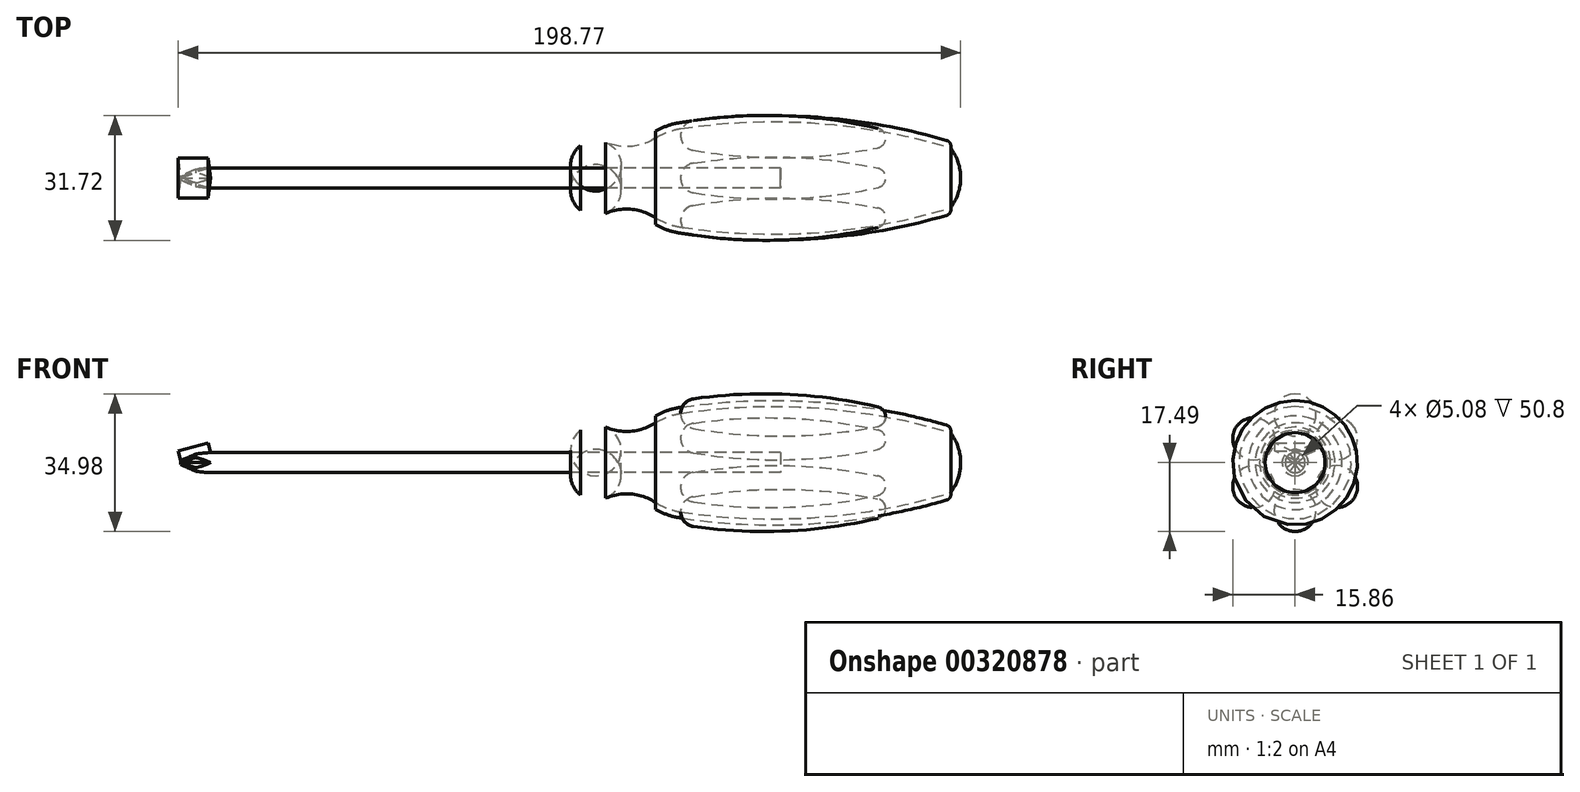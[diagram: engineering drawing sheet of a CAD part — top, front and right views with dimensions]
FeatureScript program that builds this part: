
annotation { "Feature Type Name" : "Feature", "Feature Type Description" : "" }
export const myFeature = defineFeature(function(context is Context, id is Id, definition is map)
    precondition{}
    {
        {
            var Q0;
            Q0=qCreatedBy(makeId("Front.planeOp"),FACE);
            var sketch = newSketch(context, id + "F0", { "sketchPlane" : qUnion([Q0])});
            skLineSegment(sketch, "E0", {"start": v(-101.6, 0) * mm, "end": v(96.52, 0) * mm});
            skLineSegment(sketch, "E1", {"start": v(96.52, 0) * mm, "end": v(117.55, 0) * mm, "construction": true});
            skLineSegment(sketch, "E2", {"start": v(50.8, 2.54) * mm, "end": v(-97.8, 2.54) * mm});
            skLineSegment(sketch, "E3", {"start": v(-101.6, 0.5) * mm, "end": v(-101.6, 0) * mm});
            skLineSegment(sketch, "E4", {"start": v(0, 2.54) * mm, "end": v(0, 8.25) * mm});
            skArc(sketch, "E5", {"start": v(6.35, 9.02) * mm, "mid": v(3.07, 9.48) * mm, "end": v(0, 8.25) * mm});
            skArc(sketch, "E6", {"start": v(6.35, 9.02) * mm, "mid": v(12.84, 7.99) * mm, "end": v(19.05, 10.11) * mm});
            skArc(sketch, "E7", {"start": v(25.4, 12.52) * mm, "mid": v(22.1, 11.65) * mm, "end": v(19.05, 10.11) * mm});
            skArc(sketch, "E8", {"start": v(93.98, 7.62) * mm, "mid": v(59.96, 13.9) * mm, "end": v(25.4, 12.52) * mm});
            skArc(sketch, "E9", {"start": v(96.52, 0) * mm, "mid": v(95.87, 4.02) * mm, "end": v(93.98, 7.62) * mm});
            skArc(sketch, "E10.0", {"start": v(25.17, 14.02) * mm, "mid": v(22.01, 13.24) * mm, "end": v(19.05, 11.9) * mm});
            skArc(sketch, "E10.1", {"start": v(92.95, 9.52) * mm, "mid": v(59.3, 15.46) * mm, "end": v(25.17, 14.02) * mm});
            skLineSegment(sketch, "E11", {"start": v(19.05, 11.9) * mm, "end": v(19.05, 10.11) * mm});
            skArc(sketch, "E12", {"start": v(93.98, 7.62) * mm, "mid": v(93.86, 8.78) * mm, "end": v(92.95, 9.52) * mm});
            skPoint(sketch, "E13.orphan", {"position": v(0, 0) * mm});
            skLineSegment(sketch, "E14", {"start": v(50.8, 2.54) * mm, "end": v(50.8, 0) * mm});
            skLineSegment(sketch, "E15", {"start": v(-101.6, 0.5) * mm, "end": v(-97.8, 2.54) * mm});
            skPoint(sketch, "E16.orphan", {"position": v(-101.6, 2.54) * mm});
            skSolve(sketch);
        }
        {
            var Q0;
            Q0=qCreatedBy(makeId("Front.planeOp"),FACE);
            var sketch = newSketch(context, id + "F1", { "sketchPlane" : qUnion([Q0])});
            skLineSegment(sketch, "E17", {"start": v(25.4, 12.52) * mm, "end": v(77.47, 11.64) * mm});
            skArc(sketch, "E18", {"start": v(28.67, 16.22) * mm, "mid": v(26.35, 14.97) * mm, "end": v(25.4, 12.52) * mm});
            skArc(sketch, "E19", {"start": v(77.47, 11.64) * mm, "mid": v(76.93, 13.25) * mm, "end": v(75.5, 14.16) * mm});
            skArc(sketch, "E20", {"start": v(75.5, 14.16) * mm, "mid": v(52.19, 17.37) * mm, "end": v(28.67, 16.22) * mm});
            skSolve(sketch);
        }
        {
            var Q0;
            Q0=qCreatedBy(makeId("Front.planeOp"),FACE);
            var sketch = newSketch(context, id + "F2", { "sketchPlane" : qUnion([Q0])});
            skLineSegment(sketch, "E21", {"start": v(-101.6, 0.5) * mm, "end": v(-93.98, 2.54) * mm});
            skSolve(sketch);
        }
        {
            var Q0;
            Q0=sQuery(id+"F2.wireOp",VERTEX,"E21.start");
            var Q1;
            Q1=sQuery(id+"F2.wireOp",EDGE,"E21");
            cPlane(context, id + "F3", {"entities" : qUnion([Q0, Q1]), "cplaneType" : CPlaneType.LINE_POINT, "offset" : 25.4 * mm, "width" : 152.4 * mm, "height" : 152.4 * mm});
        }
        {
            var Q0;
            Q0=qCreatedBy(id+"F3.planeOp",FACE);
            var sketch = newSketch(context, id + "F4", { "sketchPlane" : qUnion([Q0])});
            skLineSegment(sketch, "E22", {"start": v(5.08, 29.2) * mm, "end": v(0, 26.67) * mm});
            skLineSegment(sketch, "E23", {"start": v(0, 26.67) * mm, "end": v(-5.08, 29.2) * mm});
            skLineSegment(sketch, "E24", {"start": v(-5.08, 29.2) * mm, "end": v(5.08, 29.2) * mm});
            skLineSegment(sketch, "E25", {"start": v(0, 29.2) * mm, "end": v(0, 26.67) * mm, "construction": true});
            skSolve(sketch);
        }
        {
            var Q0;
            {var subQ0=sQuery(id+"F0.wireOp",EDGE,"E3");Q0=makeQuery(id+"F0.imprint","IMPRINT",FACE,{"disambiguationData":[TD([[makeQuery(id+"F0.imprint","IMPRINT",EDGE,{"derivedFrom":subQ0}),1.0]])]});}
            var Q1;
            Q1=sQuery(id+"F0.wireOp",EDGE,"E1");
            revolve(context, id + "F5", {"entities" : qUnion([Q0]), "axis" : qUnion([Q1]), "revolveType" : RevolveType.FULL});
        }
        {
            var Q0;
            {var subQ0=sQuery(id+"F0.wireOp",EDGE,"E4");Q0=makeQuery(id+"F0.imprint","IMPRINT",FACE,{"disambiguationData":[TD([[makeQuery(id+"F0.imprint","IMPRINT",EDGE,{"derivedFrom":subQ0}),-1.0]])]});}
            var Q1;
            Q1=sQuery(id+"F0.wireOp",EDGE,"E1");
            revolve(context, id + "F6", {"entities" : qUnion([Q0]), "axis" : qUnion([Q1]), "revolveType" : RevolveType.FULL});
        }
        {
            var Q0;
            Q0=makeQuery(id+"F1.imprint","IMPRINT",FACE,{"disambiguationData":[TD([[makeQuery(id+"F1.imprint","IMPRINT",EDGE,{"derivedFrom":sQuery(id+"F1.wireOp",EDGE,"E17")}),1.0]])]});
            var Q1;
            Q1=sQuery(id+"F1.wireOp",EDGE,"E17");
            revolve(context, id + "F7", {"entities" : qUnion([Q0]), "axis" : qUnion([Q1]), "revolveType" : RevolveType.FULL});
        }
        {
            var Q0;
            Q0=makeQuery(id+"F7.opRevolve","SWEPT_BODY",BODY,{"disambiguationData":[OSD([sQuery(id+"F1.wireOp",EDGE,"E17"),sQuery(id+"F1.wireOp",EDGE,"E18"),sQuery(id+"F1.wireOp",EDGE,"E19"),sQuery(id+"F1.wireOp",EDGE,"E20")])]});
            var Q1;
            Q1=sQuery(id+"F0.wireOp",EDGE,"E1");
            circularPattern(context, id + "F8", {"entities" : qUnion([Q0]), "axis" : qUnion([Q1]), "angle" : 360 * degree, "instanceCount" : 6, "equalSpace" : true});
        }
        {
            var Q0;
            Q0=makeQuery(id+"F0.imprint","IMPRINT",FACE,{"disambiguationData":[TD([[makeQuery(id+"F0.imprint","IMPRINT",EDGE,{"derivedFrom":sQuery(id+"F0.wireOp",EDGE,"E7")}),-1.0]])]});
            var Q1;
            Q1=sQuery(id+"F0.wireOp",EDGE,"E1");
            revolve(context, id + "F9", {"entities" : qUnion([Q0]), "axis" : qUnion([Q1]), "revolveType" : RevolveType.FULL});
        }
        {
            var Q0;
            Q0=makeQuery(id+"F6.opRevolve","SWEPT_BODY",BODY,{"disambiguationData":[OSD([sQuery(id+"F0.wireOp",EDGE,"E0"),sQuery(id+"F0.wireOp",EDGE,"E2"),sQuery(id+"F0.wireOp",EDGE,"E4"),sQuery(id+"F0.wireOp",EDGE,"E5"),sQuery(id+"F0.wireOp",EDGE,"E6"),sQuery(id+"F0.wireOp",EDGE,"E7"),sQuery(id+"F0.wireOp",EDGE,"E8"),sQuery(id+"F0.wireOp",EDGE,"E9"),sQuery(id+"F0.wireOp",EDGE,"E14")])]});
            var Q1;
            Q1=makeQuery(id+"F9.opRevolve","SWEPT_BODY",BODY,{"disambiguationData":[OSD([sQuery(id+"F0.wireOp",EDGE,"E7"),sQuery(id+"F0.wireOp",EDGE,"E8"),sQuery(id+"F0.wireOp",EDGE,"E10.0"),sQuery(id+"F0.wireOp",EDGE,"E10.1"),sQuery(id+"F0.wireOp",EDGE,"E11"),sQuery(id+"F0.wireOp",EDGE,"E12")])]});
            booleanBodies(context, id + "F10", {"operationType" : BooleanOperationType.SUBTRACTION, "tools" : qUnion([Q0]), "targets" : qUnion([Q1]), "keepTools" : true});
        }
        {
            var Q0;
            Q0=makeQuery(id+"F4.imprint","IMPRINT",FACE,{"disambiguationData":[TD([[makeQuery(id+"F4.imprint","IMPRINT",EDGE,{"derivedFrom":sQuery(id+"F4.wireOp",EDGE,"E22")}),-1.0]])]});
            var Q1;
            Q1=sQuery(id+"F2.wireOp",EDGE,"E21");
            sweep(context, id + "F11", {"operationType" : NewBodyOperationType.REMOVE, "profiles" : qUnion([Q0]), "path" : qUnion([Q1])});
        }
        {
            var Q0;
            Q0=makeQuery(id+"F11.boolean.opBoolean","COPY",FACE,{"derivedFrom":makeQuery(id+"F11.opSweep","SWEPT_FACE",FACE,{"disambiguationData":[OSD([sQuery(id+"F2.wireOp",EDGE,"E21"),sQuery(id+"F4.wireOp",EDGE,"E23")])]})});
            var Q1;
            Q1=makeQuery(id+"F11.boolean.opBoolean","COPY",FACE,{"derivedFrom":makeQuery(id+"F11.opSweep","SWEPT_FACE",FACE,{"disambiguationData":[OSD([sQuery(id+"F2.wireOp",EDGE,"E21"),sQuery(id+"F4.wireOp",EDGE,"E22")])]})});
            var Q2;
            Q2=sQuery(id+"F0.wireOp",EDGE,"E1");
            circularPattern(context, id + "F12", {"patternType" : PatternType.FACE, "faces" : qUnion([Q0, Q1]), "axis" : qUnion([Q2]), "angle" : 360 * degree, "instanceCount" : 4, "equalSpace" : true});
        }
        {
            var Q0;
            Q0=makeQuery(id+"F4.imprint","IMPRINT",FACE,{"disambiguationData":[TD([[makeQuery(id+"F4.imprint","IMPRINT",EDGE,{"derivedFrom":sQuery(id+"F4.wireOp",EDGE,"E22")}),-1.0]])]});
            var Q1;
            Q1=qConstructionFilter(qBodyType(qCreatedBy(id+"F2",EDGE),BodyType.WIRE),ConstructionObject.NO);
            sweep(context, id + "F13", {"profiles" : qUnion([Q0]), "path" : qUnion([Q1])});
        }
    });
